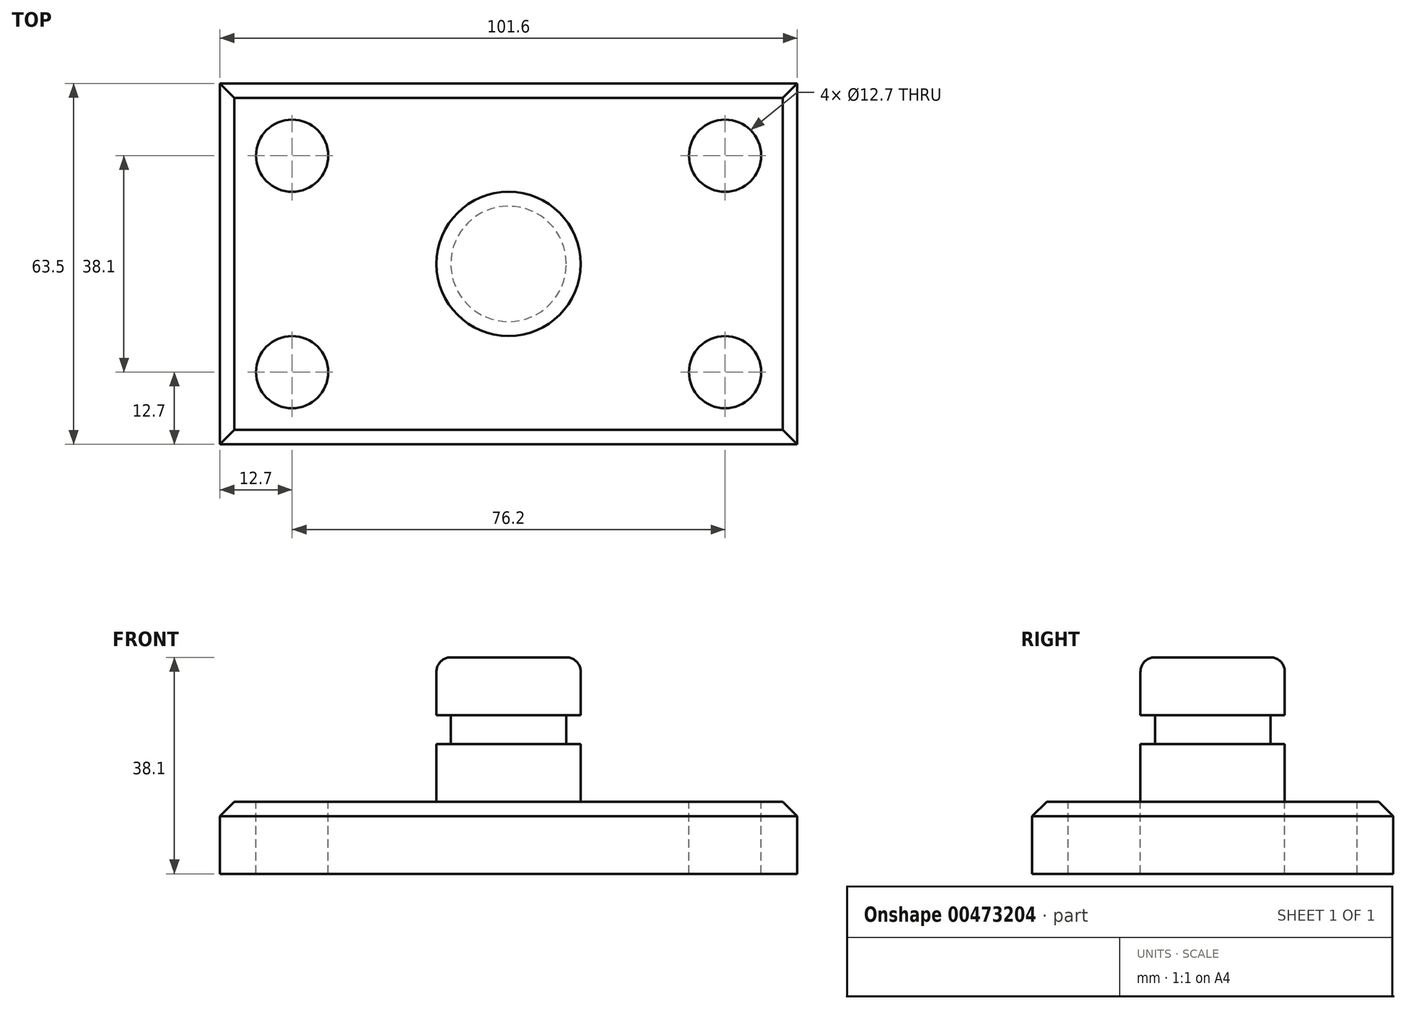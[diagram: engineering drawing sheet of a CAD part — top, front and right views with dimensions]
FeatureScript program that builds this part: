
annotation { "Feature Type Name" : "Feature", "Feature Type Description" : "" }
export const myFeature = defineFeature(function(context is Context, id is Id, definition is map)
    precondition{}
    {
        {
            var Q0;
            Q0=qCreatedBy(makeId("Top.planeOp"),FACE);
            var sketch = newSketch(context, id + "F0", { "sketchPlane" : qUnion([Q0])});
            skLineSegment(sketch, "E0.bottom", {"start": v(50.8, -31.75) * mm, "end": v(-50.8, -31.75) * mm});
            skLineSegment(sketch, "E0.top", {"start": v(50.8, 31.75) * mm, "end": v(-50.8, 31.75) * mm});
            skLineSegment(sketch, "E0.left", {"start": v(50.8, -31.75) * mm, "end": v(50.8, 31.75) * mm});
            skLineSegment(sketch, "E0.right", {"start": v(-50.8, -31.75) * mm, "end": v(-50.8, 31.75) * mm});
            skPoint(sketch, "E0.middle", {"position": v(0, 0) * mm});
            skSolve(sketch);
        }
        {
            var Q0;
            Q0=makeQuery(id+"F0.imprint","IMPRINT",FACE,{"disambiguationData":[TD([[makeQuery(id+"F0.imprint","IMPRINT",EDGE,{"derivedFrom":sQuery(id+"F0.wireOp",EDGE,"E0.bottom")}),-1.0]])]});
            extrude(context, id + "F1", {"entities" : qUnion([Q0]), "depth" : 12.7 * mm});
        }
        {
            var Q0;
            Q0=makeQuery(id+"F1.opExtrude","CAP_FACE",FACE,{"disambiguationData":[OSD([sQuery(id+"F0.wireOp",EDGE,"E0.bottom"),sQuery(id+"F0.wireOp",EDGE,"E0.top"),sQuery(id+"F0.wireOp",EDGE,"E0.left"),sQuery(id+"F0.wireOp",EDGE,"E0.right")])],"isStart":false});
            var sketch = newSketch(context, id + "F2", { "sketchPlane" : qUnion([Q0])});
            skCircle(sketch, "E1", {"center": v(-38.1, 19.05) * mm, "radius": 6.35 * mm});
            skCircle(sketch, "E2", {"center": v(38.1, 19.05) * mm, "radius": 6.35 * mm});
            skCircle(sketch, "E3", {"center": v(38.1, -19.05) * mm, "radius": 6.35 * mm});
            skCircle(sketch, "E4", {"center": v(-38.1, -19.05) * mm, "radius": 6.35 * mm});
            skSolve(sketch);
        }
        {
            var Q0;
            Q0 = qSketchRegion(id + "F2", true);
            extrude(context, id + "F3", {"entities" : qUnion([Q0]), "operationType" : NewBodyOperationType.REMOVE, "endBound" : BoundingType.THROUGH_ALL, "oppositeDirection" : true, "depth" : 25.4 * mm});
        }
        {
            var Q0;
            Q0=qCreatedBy(makeId("Front.planeOp"),FACE);
            var sketch = newSketch(context, id + "F4", { "sketchPlane" : qUnion([Q0])});
            skLineSegment(sketch, "E5.bottom", {"start": v(0, 12.7) * mm, "end": v(12.7, 12.7) * mm});
            skLineSegment(sketch, "E5.top", {"start": v(0, 38.1) * mm, "end": v(12.7, 38.1) * mm});
            skLineSegment(sketch, "E5.left", {"start": v(0, 12.7) * mm, "end": v(0, 38.1) * mm});
            skLineSegment(sketch, "E5.right", {"start": v(12.7, 12.7) * mm, "end": v(12.7, 38.1) * mm});
            skSolve(sketch);
        }
        {
            var Q0;
            Q0=makeQuery(id+"F4.imprint","IMPRINT",FACE,{"disambiguationData":[TD([[makeQuery(id+"F4.imprint","IMPRINT",EDGE,{"derivedFrom":sQuery(id+"F4.wireOp",EDGE,"E5.bottom")}),1.0]])]});
            var Q1;
            Q1=sQuery(id+"F4.wireOp",EDGE,"E5.left");
            revolve(context, id + "F5", {"operationType" : NewBodyOperationType.ADD, "entities" : qUnion([Q0]), "axis" : qUnion([Q1]), "revolveType" : RevolveType.FULL});
        }
        {
            var Q0;
            Q0=qCreatedBy(makeId("Front.planeOp"),FACE);
            var sketch = newSketch(context, id + "F6", { "sketchPlane" : qUnion([Q0])});
            skLineSegment(sketch, "E6.bottom", {"start": v(15.24, 27.94) * mm, "end": v(10.16, 27.94) * mm});
            skLineSegment(sketch, "E6.top", {"start": v(15.24, 22.86) * mm, "end": v(10.16, 22.86) * mm});
            skLineSegment(sketch, "E6.left", {"start": v(15.24, 27.94) * mm, "end": v(15.24, 22.86) * mm});
            skLineSegment(sketch, "E6.right", {"start": v(10.16, 27.94) * mm, "end": v(10.16, 22.86) * mm});
            skSolve(sketch);
        }
        {
            var Q0;
            Q0=makeQuery(id+"F6.imprint","IMPRINT",FACE,{"disambiguationData":[TD([[makeQuery(id+"F6.imprint","IMPRINT",EDGE,{"derivedFrom":sQuery(id+"F6.wireOp",EDGE,"E6.bottom")}),1.0]])]});
            var Q1;
            Q1=makeQuery(id+"F5.opRevolve","SWEPT_FACE",FACE,{"disambiguationData":[OSD([sQuery(id+"F4.wireOp",EDGE,"E5.right")])]});
            revolve(context, id + "F7", {"operationType" : NewBodyOperationType.REMOVE, "entities" : qUnion([Q0]), "axis" : qUnion([Q1]), "revolveType" : RevolveType.FULL, "oppositeDirection" : true});
        }
        {
            var Q0;
            Q0=makeQuery(id+"F5.opRevolve","SWEPT_EDGE",EDGE,{"disambiguationData":[OSD([sQuery(id+"F4.wireOp",EDGE,"E5.bottom"),sQuery(id+"F4.wireOp",EDGE,"E5.right")])]});
            var Q1;
            Q1=makeQuery(id+"F5.opRevolve","SWEPT_EDGE",EDGE,{"disambiguationData":[OSD([sQuery(id+"F4.wireOp",EDGE,"E5.top"),sQuery(id+"F4.wireOp",EDGE,"E5.right")])]});
            fillet(context, id + "F8", {"entities" : qUnion([Q0, Q1]), "radius" : 2.54 * mm, "tangentPropagation" : true, "allowEdgeOverflow" : false});
        }
        {
            var Q0;
            Q0=makeQuery(id+"F1.opExtrude","CAP_EDGE",EDGE,{"disambiguationData":[OSD([sQuery(id+"F0.wireOp",EDGE,"E0.bottom")])],"isStart":false});
            var Q1;
            Q1=makeQuery(id+"F1.opExtrude","CAP_EDGE",EDGE,{"disambiguationData":[OSD([sQuery(id+"F0.wireOp",EDGE,"E0.left")])],"isStart":false});
            var Q2;
            Q2=makeQuery(id+"F1.opExtrude","CAP_EDGE",EDGE,{"disambiguationData":[OSD([sQuery(id+"F0.wireOp",EDGE,"E0.top")])],"isStart":false});
            var Q3;
            Q3=makeQuery(id+"F1.opExtrude","CAP_EDGE",EDGE,{"disambiguationData":[OSD([sQuery(id+"F0.wireOp",EDGE,"E0.right")])],"isStart":false});
            chamfer(context, id + "F9", {"entities" : qUnion([Q0, Q1, Q2, Q3]), "width" : 2.54 * mm, "tangentPropagation" : true});
        }
    });
